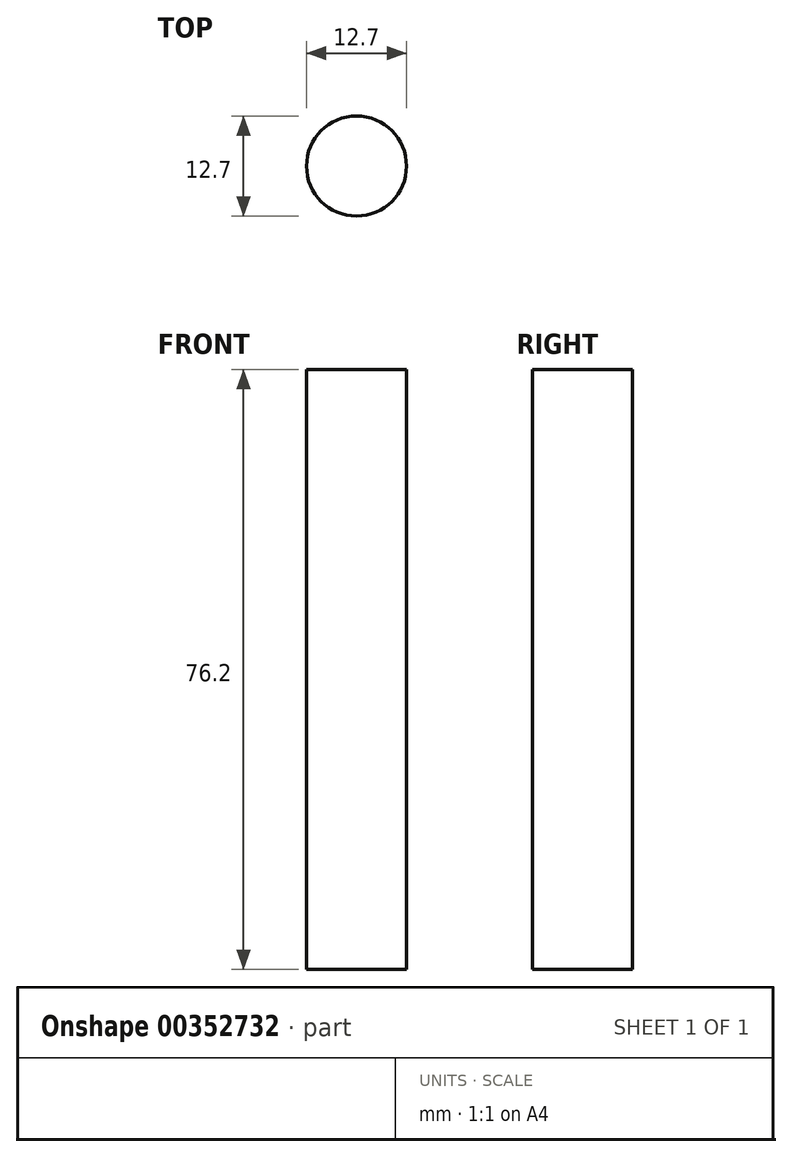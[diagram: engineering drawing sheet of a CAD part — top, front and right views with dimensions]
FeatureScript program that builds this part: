
annotation { "Feature Type Name" : "Feature", "Feature Type Description" : "" }
export const myFeature = defineFeature(function(context is Context, id is Id, definition is map)
    precondition{}
    {
        {
            var Q0;
            Q0=qCreatedBy(makeId("Front.planeOp"),FACE);
            var sketch = newSketch(context, id + "F0", { "sketchPlane" : qUnion([Q0])});
            skLineSegment(sketch, "E0.bottom", {"start": v(0, 0) * mm, "end": v(-6.35, 0) * mm});
            skLineSegment(sketch, "E0.top", {"start": v(0, -76.2) * mm, "end": v(-6.35, -76.2) * mm});
            skLineSegment(sketch, "E0.left", {"start": v(0, 0) * mm, "end": v(0, -76.2) * mm});
            skLineSegment(sketch, "E0.right", {"start": v(-6.35, 0) * mm, "end": v(-6.35, -76.2) * mm});
            skSolve(sketch);
        }
        {
            var Q0;
            Q0=makeQuery(id+"F0.imprint","IMPRINT",FACE,{"disambiguationData":[TD([[makeQuery(id+"F0.imprint","IMPRINT",EDGE,{"derivedFrom":sQuery(id+"F0.wireOp",EDGE,"E0.bottom")}),1.0]])]});
            var Q1;
            Q1=sQuery(id+"F0.wireOp",EDGE,"E0.left");
            revolve(context, id + "F1", {"entities" : qUnion([Q0]), "axis" : qUnion([Q1]), "revolveType" : RevolveType.FULL});
        }
    });
